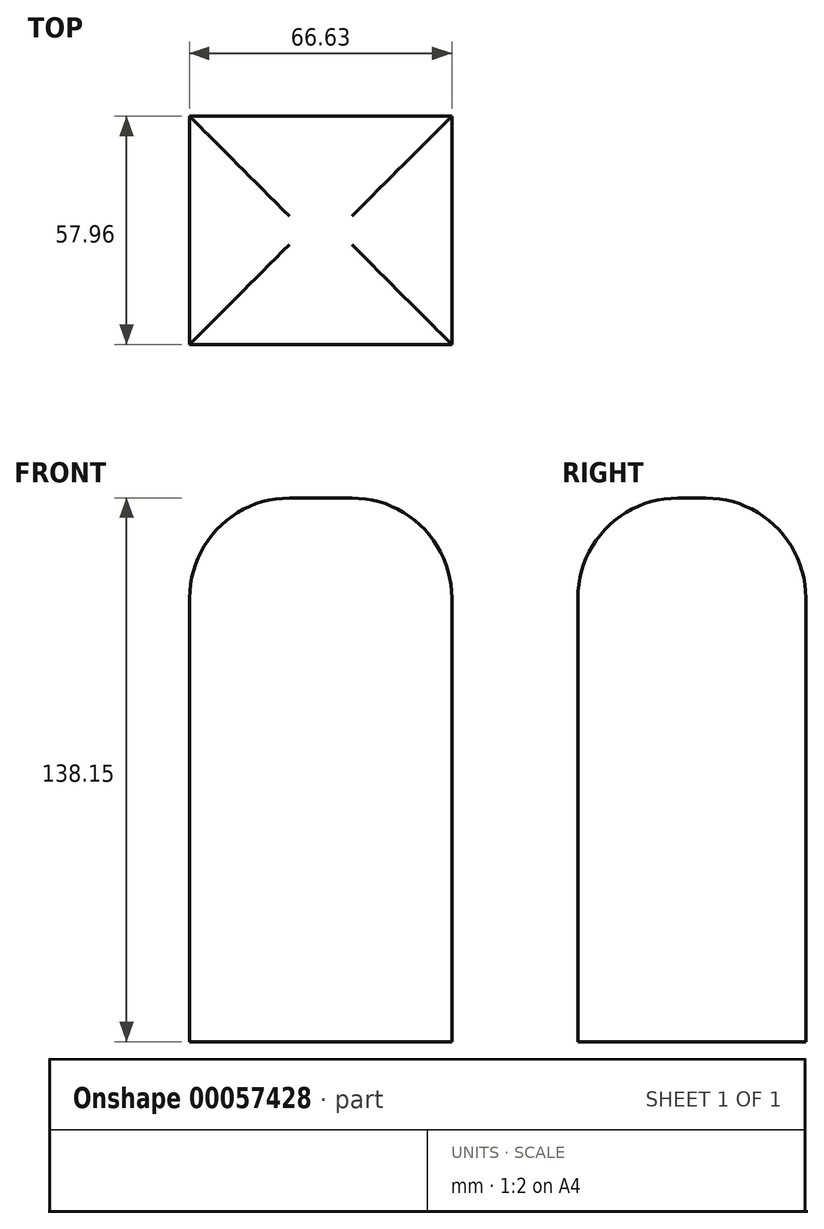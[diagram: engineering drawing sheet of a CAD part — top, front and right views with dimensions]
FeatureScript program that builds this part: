
annotation { "Feature Type Name" : "Feature", "Feature Type Description" : "" }
export const myFeature = defineFeature(function(context is Context, id is Id, definition is map)
    precondition{}
    {
        {
            var Q0;
            Q0=qCreatedBy(makeId("Top.planeOp"),FACE);
            var sketch = newSketch(context, id + "F0", { "sketchPlane" : qUnion([Q0])});
            skLineSegment(sketch, "E0.bottom", {"start": v(0, 0) * mm, "end": v(66.63, 0) * mm});
            skLineSegment(sketch, "E0.top", {"start": v(0, -57.96) * mm, "end": v(66.63, -57.96) * mm});
            skLineSegment(sketch, "E0.left", {"start": v(0, 0) * mm, "end": v(0, -57.96) * mm});
            skLineSegment(sketch, "E0.right", {"start": v(66.63, 0) * mm, "end": v(66.63, -57.96) * mm});
            skSolve(sketch);
        }
        {
            var Q0;
            Q0=makeQuery(id+"F0.imprint","IMPRINT",FACE,{"disambiguationData":[TD([[makeQuery(id+"F0.imprint","IMPRINT",EDGE,{"derivedFrom":sQuery(id+"F0.wireOp",EDGE,"E0.bottom")}),-1.0]])]});
            extrude(context, id + "F1", {"entities" : qUnion([Q0]), "depth" : 138.15 * mm});
        }
        {
            var Q0;
            Q0=makeQuery(id+"F1.opExtrude","CAP_EDGE",EDGE,{"disambiguationData":[OSD([sQuery(id+"F0.wireOp",EDGE,"E0.top")])],"isStart":false});
            var Q1;
            Q1=makeQuery(id+"F1.opExtrude","CAP_EDGE",EDGE,{"disambiguationData":[OSD([sQuery(id+"F0.wireOp",EDGE,"E0.right")])],"isStart":false});
            var Q2;
            Q2=makeQuery(id+"F1.opExtrude","CAP_EDGE",EDGE,{"disambiguationData":[OSD([sQuery(id+"F0.wireOp",EDGE,"E0.left")])],"isStart":false});
            var Q3;
            Q3=makeQuery(id+"F1.opExtrude","CAP_EDGE",EDGE,{"disambiguationData":[OSD([sQuery(id+"F0.wireOp",EDGE,"E0.bottom")])],"isStart":false});
            fillet(context, id + "F2", {"entities" : qUnion([Q0, Q1, Q2, Q3]), "radius" : 25.4 * mm, "tangentPropagation" : true, "allowEdgeOverflow" : false});
        }
    });
